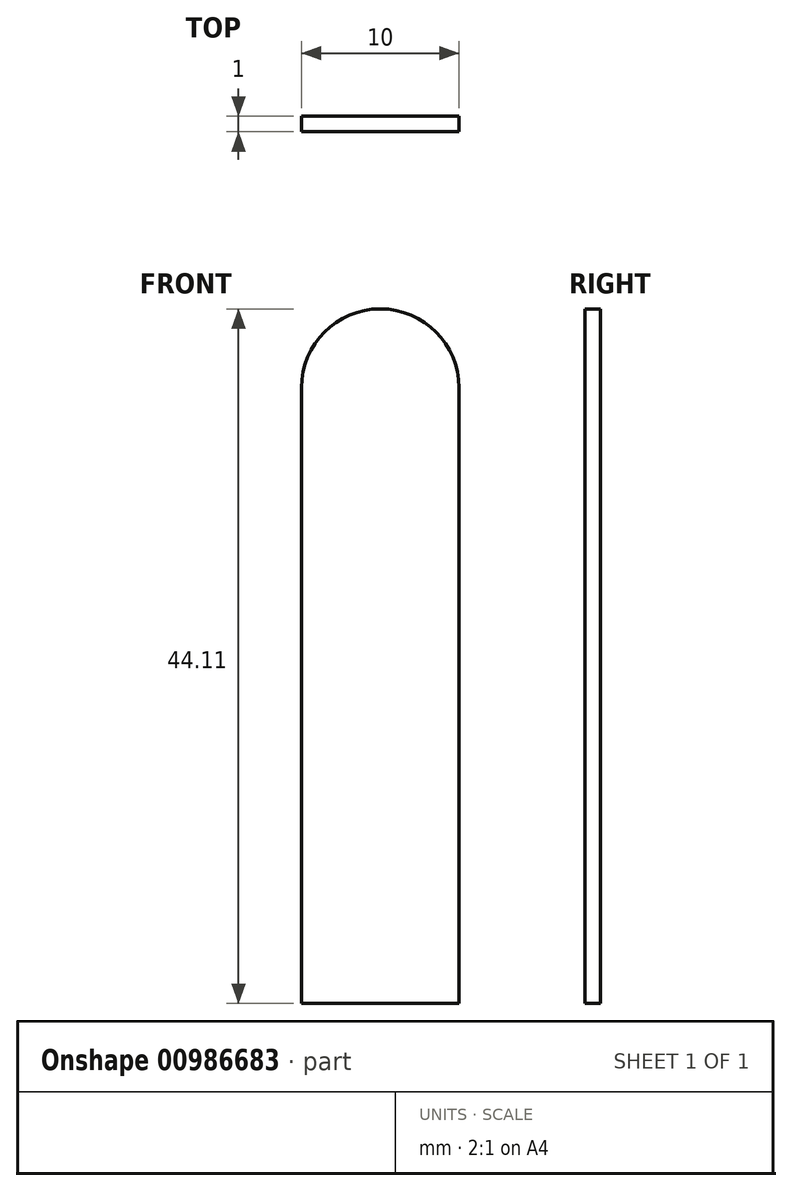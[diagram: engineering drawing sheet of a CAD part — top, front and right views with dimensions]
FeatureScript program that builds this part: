
annotation { "Feature Type Name" : "Feature", "Feature Type Description" : "" }
export const myFeature = defineFeature(function(context is Context, id is Id, definition is map)
    precondition{}
    {
        {
            var Q0;
            Q0=qCreatedBy(makeId("Front.planeOp"),FACE);
            var sketch = newSketch(context, id + "F0", { "sketchPlane" : qUnion([Q0])});
            skLineSegment(sketch, "E0.bottom", {"start": v(0, 0) * mm, "end": v(66.63, 0) * mm});
            skLineSegment(sketch, "E0.top", {"start": v(0, 62.27) * mm, "end": v(66.63, 62.27) * mm});
            skLineSegment(sketch, "E0.left", {"start": v(0, 0) * mm, "end": v(0, 62.27) * mm});
            skLineSegment(sketch, "E0.right", {"start": v(66.63, 0) * mm, "end": v(66.63, 62.27) * mm});
            skSolve(sketch);
        }
        {
            var Q0;
            Q0=makeQuery(id+"F0.imprint","IMPRINT",FACE,{"disambiguationData":[TD([[makeQuery(id+"F0.imprint","IMPRINT",EDGE,{"derivedFrom":sQuery(id+"F0.wireOp",EDGE,"E0.bottom")}),1.0]])]});
            extrude(context, id + "F1", {"entities" : qUnion([Q0]), "depth" : 1 * mm, "offsetDistance" : 25 * mm});
        }
        {
            var Q0;
            Q0=makeQuery(id+"F1.opExtrude","CAP_FACE",FACE,{"disambiguationData":[OSD([sQuery(id+"F0.wireOp",EDGE,"E0.bottom"),sQuery(id+"F0.wireOp",EDGE,"E0.top"),sQuery(id+"F0.wireOp",EDGE,"E0.left"),sQuery(id+"F0.wireOp",EDGE,"E0.right")])],"isStart":false});
            var sketch = newSketch(context, id + "F2", { "sketchPlane" : qUnion([Q0])});
            skLineSegment(sketch, "E1", {"start": v(31.35, 0) * mm, "end": v(31.35, 39.11) * mm});
            skArc(sketch, "E2.0.startCap", {"start": v(36.35, 0) * mm, "mid": v(31.35, -5) * mm, "end": v(26.35, 0) * mm});
            skArc(sketch, "E2.0.endCap", {"start": v(26.35, 39.11) * mm, "mid": v(31.35, 44.11) * mm, "end": v(36.35, 39.11) * mm});
            skLineSegment(sketch, "E2.0.left", {"start": v(26.35, 0) * mm, "end": v(26.35, 39.11) * mm});
            skLineSegment(sketch, "E2.0.right", {"start": v(36.35, 0) * mm, "end": v(36.35, 39.11) * mm});
            skSolve(sketch);
        }
        {
            var Q0;
            Q0=makeQuery(id+"F2.imprint","IMPRINT",FACE,{"disambiguationData":[TD([[makeQuery(id+"F2.imprint","IMPRINT",EDGE,{"derivedFrom":sQuery(id+"F2.wireOp",EDGE,"E2.0.endCap")}),-1.0]])]});
            extrude(context, id + "F3", {"entities" : qUnion([Q0]), "operationType" : NewBodyOperationType.REMOVE, "endBound" : BoundingType.THROUGH_ALL, "oppositeDirection" : true, "depth" : 25 * mm, "offsetDistance" : 25 * mm});
        }
    });
